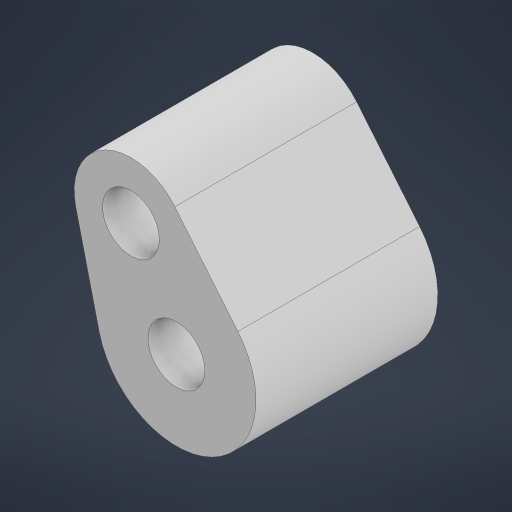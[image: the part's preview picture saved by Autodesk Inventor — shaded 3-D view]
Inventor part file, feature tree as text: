
AUTODESK INVENTOR PART (.ipt)
format: ipt  version: 2024 (Build 280153000, 153)  size: 186,368 bytes
history: native  units: in
note: dims shown in document units (in); Inventor stores cm internally (conversion verified against a paired STEP export)
features: extrude x1, sketch x1
ambient origin geometry x8: Origin, YZ Plane, XZ Plane, XY Plane, X Axis, Y Axis, Z Axis, Center Point
bodies: Solid1 (feature_tree)
feature tree (2):
  extrude  "Extrusion1"  Depth=1.0in
  sketch  "Sketch1"  dims[d0=0.5in d1=0.25in d2=0.3125in d3=0.3125in d4=0.625in d5=0.875in d6=1.0in d7=0.0in]
